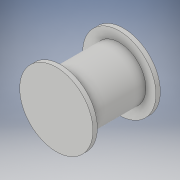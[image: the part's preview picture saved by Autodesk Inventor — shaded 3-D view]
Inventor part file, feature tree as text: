
AUTODESK INVENTOR PART (.ipt)
format: ipt  version: 2019 (Build 230136000, 136)  size: 119,296 bytes
history: native  units: mm
features: extrude x3, sketch x3, other x1
ambient origin geometry x8: Origin, YZ Plane, XZ Plane, XY Plane, X Axis, Y Axis, Z Axis, Center Point
bodies: Body1 (feature_tree)
feature tree (7):
  other  "ソリッド1"
  extrude  "押し出し1"  Depth=50.0mm
  extrude  "押し出し2"  Depth=3.0mm TaperAngle=0.0deg
  extrude  "押し出し3"  Depth=36.26mm
  sketch  "スケッチ1"
  sketch  "スケッチ2"
  sketch  "スケッチ3"
